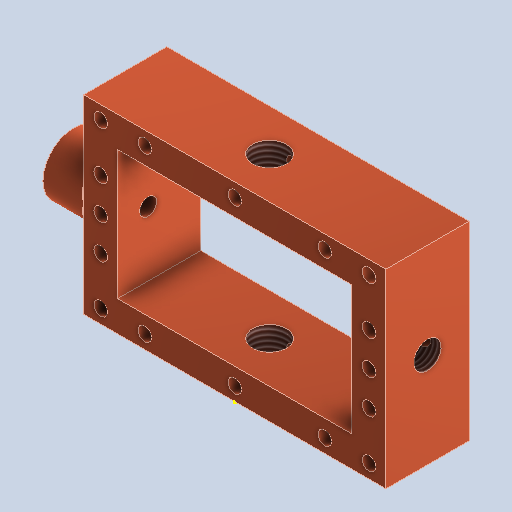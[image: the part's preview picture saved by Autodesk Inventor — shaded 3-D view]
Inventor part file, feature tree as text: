
AUTODESK INVENTOR PART (.ipt)
format: ipt  version: 2025.1 (Build 291241000, 241)  size: 243,200 bytes
history: native  units: mm
features: sketch x9, other x3, plane x2
ambient origin geometry x8: Origin, YZ Plane, XZ Plane, XY Plane, X Axis, Y Axis, Z Axis, Center Point
bodies: Volumenkörper1 (feature_tree)
feature tree (14):
  other  "1152_body.ipt"
  other  "Volumenkörper1::1152_body.ipt"
  other  "TaggingFeature1"
  sketch  "Skizze1"  dims[d0=10.0mm]
  sketch  "Skizze2"
  sketch  "Skizze3"
  sketch  "Skizze4"
  sketch  "Skizze5"
  sketch  "Skizze6"
  sketch  "Skizze7"
  sketch  "Skizze9"
  sketch  "Skizze10"
  plane  "Arbeitsebene1"
  plane  "Arbeitsebene3"
